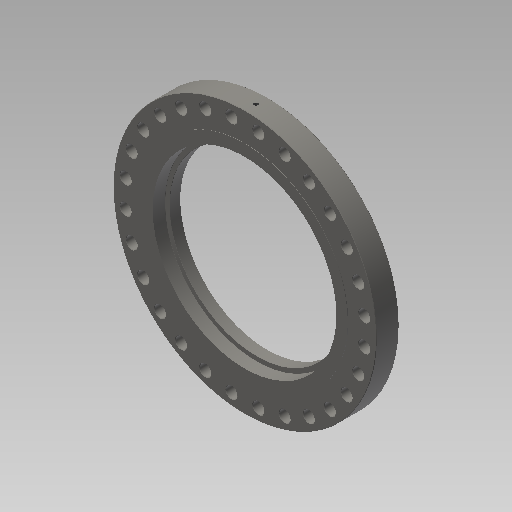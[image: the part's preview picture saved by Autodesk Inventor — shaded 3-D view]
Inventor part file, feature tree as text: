
AUTODESK INVENTOR PART (.ipt)
format: ipt  version: 2017.3 (Build 213257000, 257)  size: 331,264 bytes
history: native  units: in
note: dims shown in document units (in); Inventor stores cm internally (conversion verified against a paired STEP export)
features: sketch x6, extrude x4, chamfer x3, hole x2, pattern_circular x2, fillet x1, plane x1, projected_geometry x1
ambient origin geometry x8: Origin, YZ Plane, XZ Plane, XY Plane, X Axis, Y Axis, Z Axis, Center Point
bodies: Solid1 (feature_tree)
feature tree (20):
  extrude  "Extrusion: OD"  Depth=3.6777in TaperAngle=0.0deg
  extrude  "Extrusion: RF"  Depth=0.0625in TaperAngle=0.0deg
  extrude  "Extrusion: ID Large"  Depth=2.0in TaperAngle=0.0deg
  extrude  "Extrusion: ID Small"  Depth=39.25in
  hole  "Hole: Bolt"  [1 undecoded]
  chamfer  "Chamfer: Bolt hole"  Distance=0.0625in Angle=45.0deg
  pattern_circular  "Circular Pattern: Bolt hole"  Angle=45.0deg  [1 undecoded]
  chamfer  "Chamfer: OD"  Distance=0.0312in
  chamfer  "Chamfer2"  [1 undecoded]
  fillet  "Fillet2"  Radius=0.0625in
  plane  "Work Plane1"
  hole  "Hole2"  [1 undecoded]
  pattern_circular  "Circular Pattern2"  Count=2 Angle=360.0deg
  sketch  "Sketch1"  dims[d0=43.0in d1=3.6777in d2=0.0in]
  sketch  "Sketch2"  dims[d3=33.75in d4=0.0625in d5=0.0in]
  sketch  "Sketch3"  dims[d6=30.0in d7=2.0in d8=0.0in]
  sketch  "Sketch4"  dims[d10=2.0in d11=0.0in d12=39.25in]
  sketch  "Sketch5"  dims[d13=0.0442in]
  sketch  "Sketch6"  dims[d14=1.875in d15=0.75in d16=0.375in d17=0.25in d18=0.5635in d19=1.0in d20=0.8108in d21=11.0236in d22=360.0deg d24=0.0625in d25=0.125in d26=45.0deg d28=0.0312in d29=0.125in d30=45.0deg d31=0.0312in d32=0.0in d33=0.0625in d34=0.125in d35=45.0deg d36=1.8701in d37=0.642in d38=2.0in d39=0.375in d40=0.25in d41=0.5635in d42=2.5in d43=0.8108in d44=0.7874in d45=360.0deg]
  projected_geometry  "Projected Loop1"
note: 4 required parameter values undecoded (feature->parameter linkage not recoverable at this tier; creation-order binding heuristic only, values carry confidence <= 0.55)
